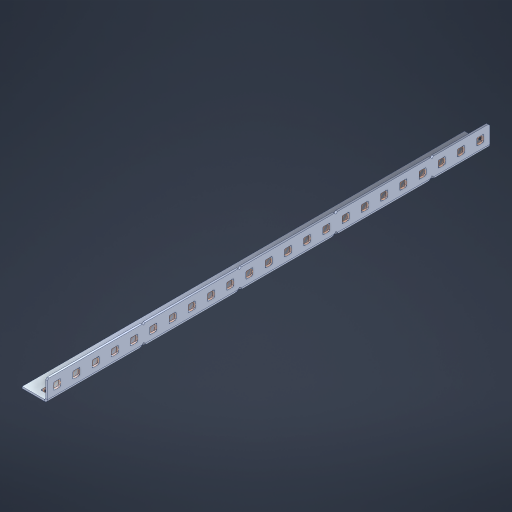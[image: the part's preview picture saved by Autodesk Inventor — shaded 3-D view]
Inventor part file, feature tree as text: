
AUTODESK INVENTOR PART (.ipt)
format: ipt  version: 2023 (Build 270158000, 158)  size: 813,568 bytes
history: native  units: in
note: dims shown in document units (in); Inventor stores cm internally (conversion verified against a paired STEP export)
features: other x51, extrude x45, sheet_metal_op x10, sketch x8, mirror x1, pattern_linear x1, chamfer x1
ambient origin geometry x8: Origin, YZ Plane, XZ Plane, XY Plane, X Axis, Y Axis, Z Axis, Center Point
bodies: Solid1 (feature_tree), Body (feature_tree)
feature tree (117):
  other  "Flange Pattern Plane"
  sheet_metal_op  "Flange Pattern"
  sheet_metal_op  "Body Pattern"
  other  "Arc Length"
  mirror  "Notch Mirror"
  pattern_linear  "Notch Pattern"  Spacing1=0.1875in  [1 undecoded]
  chamfer  "End Chamfer"
  extrude  "Half Cut"  Depth=0.0469in
  sketch  "Sketch1"  dims[d0=2.5in]
  other  "Plate1"
  sketch  "Sketch2"  dims[d1=11.5in]
  other  "Plate2"
  sheet_metal_op  "Bend1"
  sheet_metal_op  "Corner1"
  sketch  "Sketch3"  dims[d2=0.0469in]
  other  "Flange Pattern Sketch"
  sketch  "Sketch7"  dims[d3=0.0469in]
  other  "Srf1"
  other  "Srf2"
  sketch  "Sketch8"  dims[d4=0.0234in]
  sketch  "Sketch9"  dims[d5=0.0938in]
  other  "Srf91"
  sheet_metal_op  "Body Pattern Sketch"
  other  "Srf92"
  sketch  "Sketch13"  dims[d6=0.0469in]
  sketch  "Sketch14"  dims[d7=0.5in d8=90.0deg d9=0.0312in d10=0.1875in d11=0.0469in d12=0.0469in d16=0.182in d17=0.02in d18=0.0469in d19=0.0in d20=0.25in d21=0.25in d46=0.172in d47=1.0in d48=0.0in d49=0.182in d50=0.02in d51=0.25in d52=0.25in d53=0.0469in d54=0.0in d55=0.172in d56=1.0in d57=0.0in d60=9.0551in d62=0.5in d63=0.3937in d65=0.5in d85=0.1227in d86=0.1659in d88=0.04in d89=0.0469in d90=0.0in d91=0.04in d92=0.0491in d95=2.5in d96=0.04in d97=0.25in d98=45.0deg d101=0.0in d102=2.497in d131=0.5in d132=9.0551in d134=0.5in d139=0.5in]
  other  "Srf856"
  other  "Srf1310"
  other  "Srf1311"
  other  "Srf1312"
  other  "Srf1376"
  other  "Srf1377"
  other  "Srf1728"
  other  "Srf1755"
  other  "Srf1878"
  other  "Srf1879"
  other  "Srf1880"
  other  "Srf1881"
  other  "Srf1882"
  other  "Srf1883"
  other  "Srf1884"
  other  "Srf1885"
  other  "Srf1886"
  other  "Srf1887"
  other  "Srf1888"
  other  "Srf1889"
  other  "Srf1890"
  other  "Srf1891"
  other  "Srf1892"
  other  "Srf1893"
  other  "Srf1894"
  other  "Srf1942"
  other  "Srf1943"
  other  "Srf1944"
  other  "Srf1945"
  other  "Srf1946"
  other  "Srf1947"
  other  "Srf1948"
  other  "Srf1949"
  other  "Srf1950"
  other  "Srf1951"
  other  "Srf1952"
  other  "Srf1953"
  other  "Srf1954"
  other  "Srf1955"
  other  "Srf1956"
  other  "Srf1957"
  other  "Srf1958"
  sheet_metal_op  "Flange Stamp"
  sheet_metal_op  "Flange Circle"
  sheet_metal_op  "Body Stamp"
  sheet_metal_op  "Body Circle"
  sheet_metal_op  "Notch"
  extrude  "ExtrusionSrf2"  Depth=0.0469in
  extrude  "ExtrusionSrf92"  Depth=0.5in
  extrude  "ExtrusionSrf856"  Depth=0.02in
  extrude  "ExtrusionSrf1310"  Depth=0.0469in
  extrude  "ExtrusionSrf1311"  TaperAngle=0.0deg  [1 undecoded]
  extrude  "ExtrusionSrf1312"  Depth=0.5in
  extrude  "ExtrusionSrf1376"  Depth=0.5in
  extrude  "ExtrusionSrf1377"  Depth=0.5in
  extrude  "ExtrusionSrf1728"  Depth=0.5in TaperAngle=0.0deg
  extrude  "ExtrusionSrf1755"  Depth=0.5in
  extrude  "ExtrusionSrf1878"  Depth=0.02in
  extrude  "ExtrusionSrf1879"  Depth=0.5in
  extrude  "ExtrusionSrf1880"  Depth=0.5in
  extrude  "ExtrusionSrf1881"  Depth=0.0469in
  extrude  "ExtrusionSrf1882"  TaperAngle=0.0deg  [1 undecoded]
  extrude  "ExtrusionSrf1883"  Depth=0.5in
  extrude  "ExtrusionSrf1884"  Depth=0.5in TaperAngle=0.0deg
  extrude  "ExtrusionSrf1885"  Depth=0.5in
  extrude  "ExtrusionSrf1886"  Depth=0.5in
  extrude  "ExtrusionSrf1887"  Depth=0.5in
  extrude  "ExtrusionSrf1888"  Depth=0.5in
  extrude  "ExtrusionSrf1889"  Depth=0.5in
  extrude  "ExtrusionSrf1890"  Depth=0.0469in
  extrude  "ExtrusionSrf1891"  TaperAngle=0.0deg  [1 undecoded]
  extrude  "ExtrusionSrf1892"  Depth=0.5in
  extrude  "ExtrusionSrf1893"  Depth=0.5in
  extrude  "ExtrusionSrf1894"  Depth=0.5in
  extrude  "ExtrusionSrf1942"  Depth=0.5in TaperAngle=45.0deg
  extrude  "ExtrusionSrf1943"  TaperAngle=0.0deg  [1 undecoded]
  extrude  "ExtrusionSrf1944"  Depth=0.5in
  extrude  "ExtrusionSrf1945"  Depth=0.5in
  extrude  "ExtrusionSrf1946"  Depth=0.5in
  extrude  "ExtrusionSrf1947"  Depth=0.5in
  extrude  "ExtrusionSrf1948"  Depth=0.5in
  extrude  "ExtrusionSrf1949"  [1 undecoded]
  extrude  "ExtrusionSrf1950"  [1 undecoded]
  extrude  "ExtrusionSrf1951"  [1 undecoded]
  extrude  "ExtrusionSrf1952"  [1 undecoded]
  extrude  "ExtrusionSrf1953"  [1 undecoded]
  extrude  "ExtrusionSrf1954"  [1 undecoded]
  extrude  "ExtrusionSrf1955"  [1 undecoded]
  extrude  "ExtrusionSrf1956"  [1 undecoded]
  extrude  "ExtrusionSrf1957"  [1 undecoded]
  extrude  "ExtrusionSrf1958"  [1 undecoded]
note: 15 required parameter values undecoded (feature->parameter linkage not recoverable at this tier; creation-order binding heuristic only, values carry confidence <= 0.55)
